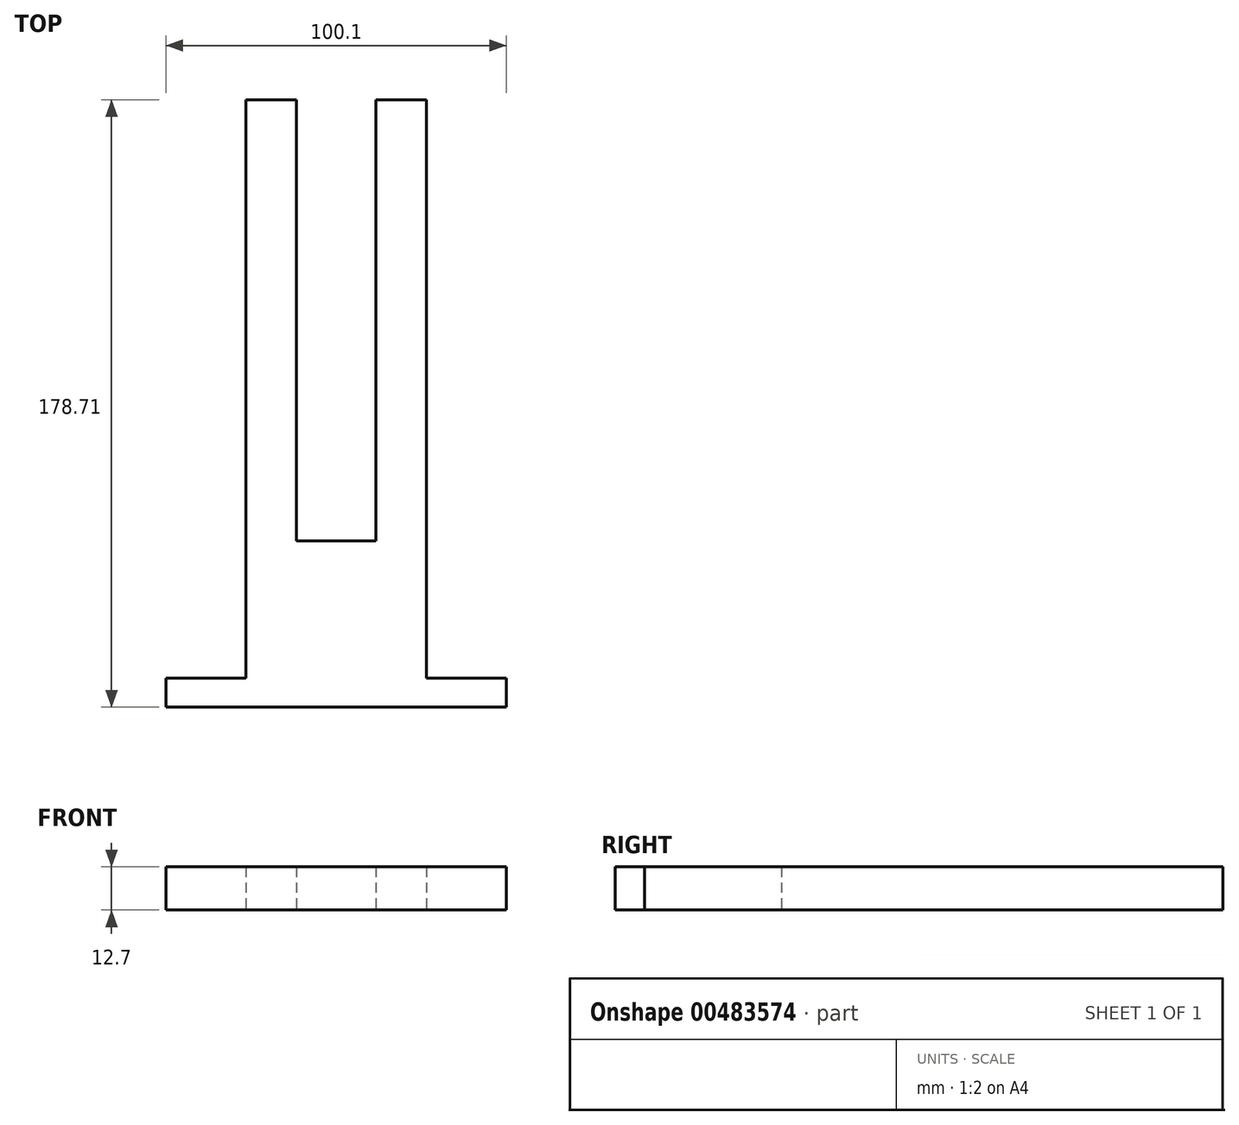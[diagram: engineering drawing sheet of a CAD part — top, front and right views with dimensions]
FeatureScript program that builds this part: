
annotation { "Feature Type Name" : "Feature", "Feature Type Description" : "" }
export const myFeature = defineFeature(function(context is Context, id is Id, definition is map)
    precondition{}
    {
        {
            var Q0;
            Q0=qCreatedBy(makeId("Top.planeOp"),FACE);
            var sketch = newSketch(context, id + "F0", { "sketchPlane" : qUnion([Q0])});
            skLineSegment(sketch, "E0", {"start": v(-41.55, 63.06) * mm, "end": v(-41.55, -107.07) * mm});
            skLineSegment(sketch, "E1", {"start": v(-41.55, -107.07) * mm, "end": v(-65.05, -107.07) * mm});
            skLineSegment(sketch, "E2", {"start": v(-65.05, -107.07) * mm, "end": v(-65.05, -115.65) * mm});
            skLineSegment(sketch, "E3", {"start": v(-65.05, -115.65) * mm, "end": v(35.05, -115.65) * mm});
            skLineSegment(sketch, "E4", {"start": v(35.05, -115.65) * mm, "end": v(35.05, -107.07) * mm});
            skLineSegment(sketch, "E5", {"start": v(35.05, -107.07) * mm, "end": v(11.55, -107.07) * mm});
            skLineSegment(sketch, "E6", {"start": v(11.55, -107.07) * mm, "end": v(11.55, 63.06) * mm});
            skLineSegment(sketch, "E7", {"start": v(11.55, 63.06) * mm, "end": v(-3.31, 63.06) * mm});
            skLineSegment(sketch, "E8", {"start": v(-41.55, 63.06) * mm, "end": v(-26.69, 63.06) * mm});
            skLineSegment(sketch, "E9", {"start": v(-26.69, 63.06) * mm, "end": v(-26.69, -66.7) * mm});
            skLineSegment(sketch, "E10", {"start": v(-3.31, 63.06) * mm, "end": v(-3.31, -66.7) * mm});
            skLineSegment(sketch, "E11", {"start": v(-26.69, -66.7) * mm, "end": v(-3.31, -66.7) * mm});
            skSolve(sketch);
        }
        {
            var Q0;
            Q0 = qSketchRegion(id + "F0", true);
            extrude(context, id + "F1", {"entities" : qUnion([Q0]), "depth" : 12.7 * mm});
        }
    });
